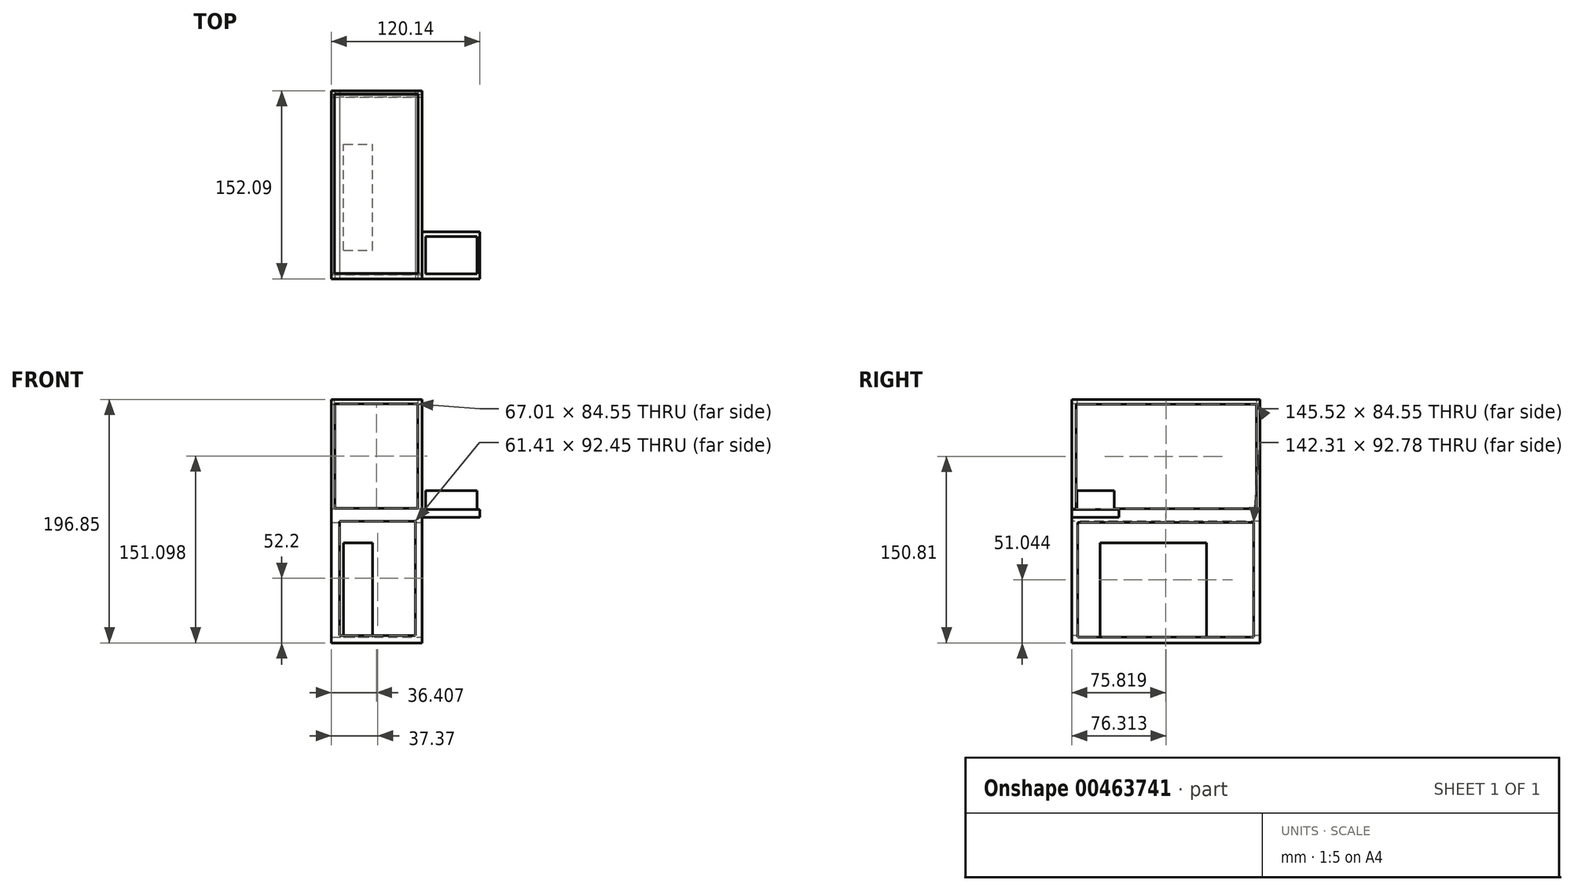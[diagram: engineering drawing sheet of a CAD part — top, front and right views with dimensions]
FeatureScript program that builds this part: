
annotation { "Feature Type Name" : "Feature", "Feature Type Description" : "" }
export const myFeature = defineFeature(function(context is Context, id is Id, definition is map)
    precondition{}
    {
        {
            var Q0;
            Q0=qCreatedBy(makeId("Top.planeOp"),FACE);
            var sketch = newSketch(context, id + "F0", { "sketchPlane" : qUnion([Q0])});
            skLineSegment(sketch, "E0", {"start": v(0, 0) * mm, "end": v(0, 75.66) * mm});
            skLineSegment(sketch, "E1", {"start": v(0, 75.66) * mm, "end": v(-73.36, 75.66) * mm});
            skLineSegment(sketch, "E2", {"start": v(-73.36, 75.66) * mm, "end": v(-73.36, -76.43) * mm});
            skLineSegment(sketch, "E3", {"start": v(-73.36, -76.43) * mm, "end": v(46.78, -76.43) * mm});
            skLineSegment(sketch, "E4", {"start": v(46.78, -76.43) * mm, "end": v(46.78, -38.34) * mm});
            skLineSegment(sketch, "E5", {"start": v(46.78, -38.34) * mm, "end": v(0, -38.34) * mm});
            skLineSegment(sketch, "E6", {"start": v(0, -38.34) * mm, "end": v(0, 0) * mm});
            skSolve(sketch);
        }
        {
            var Q0;
            Q0 = qSketchRegion(id + "F0", true);
            extrude(context, id + "F1", {"entities" : qUnion([Q0]), "depth" : 6.35 * mm});
        }
        {
            var Q0;
            Q0=makeQuery(id+"F1.opExtrude","CAP_FACE",FACE,{"disambiguationData":[OSD([sQuery(id+"F0.wireOp",EDGE,"E0"),sQuery(id+"F0.wireOp",EDGE,"E1"),sQuery(id+"F0.wireOp",EDGE,"E2"),sQuery(id+"F0.wireOp",EDGE,"E3"),sQuery(id+"F0.wireOp",EDGE,"E4"),sQuery(id+"F0.wireOp",EDGE,"E5"),sQuery(id+"F0.wireOp",EDGE,"E6")])],"isStart":false});
            var sketch = newSketch(context, id + "F2", { "sketchPlane" : qUnion([Q0])});
            skLineSegment(sketch, "E7.bottom", {"start": v(-73.36, 75.66) * mm, "end": v(0, 75.66) * mm});
            skLineSegment(sketch, "E7.top", {"start": v(-73.36, -76.43) * mm, "end": v(0, -76.43) * mm});
            skLineSegment(sketch, "E7.left", {"start": v(-73.36, 75.66) * mm, "end": v(-73.36, -76.43) * mm});
            skLineSegment(sketch, "E7.right", {"start": v(0, 75.66) * mm, "end": v(0, -76.43) * mm});
            skSolve(sketch);
        }
        {
            var Q0;
            Q0 = qSketchRegion(id + "F2", true);
            extrude(context, id + "F3", {"entities" : qUnion([Q0]), "operationType" : NewBodyOperationType.ADD, "depth" : 88.9 * mm});
        }
        {
            var Q0;
            Q0=makeQuery(id+"F3.boolean.opBoolean","MERGE",FACE,{"derivedFrom":[makeQuery(id+"F1.opExtrude","SWEPT_FACE",FACE,{"disambiguationData":[OSD([sQuery(id+"F0.wireOp",EDGE,"E3")])]}),makeQuery(id+"F3.opExtrude","SWEPT_FACE",FACE,{"disambiguationData":[OSD([sQuery(id+"F2.wireOp",EDGE,"E7.top")])]})]});
            var sketch = newSketch(context, id + "F4", { "sketchPlane" : qUnion([Q0])});
            skLineSegment(sketch, "E8.bottom", {"start": v(-70.46, 91.77) * mm, "end": v(-3.45, 91.77) * mm});
            skLineSegment(sketch, "E8.top", {"start": v(-70.46, 7.22) * mm, "end": v(-3.45, 7.22) * mm});
            skLineSegment(sketch, "E8.left", {"start": v(-70.46, 91.77) * mm, "end": v(-70.46, 7.22) * mm});
            skLineSegment(sketch, "E8.right", {"start": v(-3.45, 91.77) * mm, "end": v(-3.45, 7.22) * mm});
            skSolve(sketch);
        }
        {
            var Q0;
            Q0=makeQuery(id+"F4.imprint","IMPRINT",FACE,{"disambiguationData":[TD([[makeQuery(id+"F4.imprint","IMPRINT",EDGE,{"derivedFrom":sQuery(id+"F4.wireOp",EDGE,"E8.bottom")}),-1.0]])]});
            extrude(context, id + "F5", {"entities" : qUnion([Q0]), "operationType" : NewBodyOperationType.REMOVE, "endBound" : BoundingType.THROUGH_ALL, "oppositeDirection" : true, "depth" : 25.4 * mm});
        }
        {
            var Q0;
            Q0=makeQuery(id+"F3.boolean.opBoolean","MERGE",FACE,{"derivedFrom":[makeQuery(id+"F1.opExtrude","SWEPT_FACE",FACE,{"disambiguationData":[OSD([sQuery(id+"F0.wireOp",EDGE,"E0"),sQuery(id+"F0.wireOp",EDGE,"E6")])]}),makeQuery(id+"F3.opExtrude","SWEPT_FACE",FACE,{"disambiguationData":[OSD([sQuery(id+"F2.wireOp",EDGE,"E7.right")])]})]});
            var sketch = newSketch(context, id + "F6", { "sketchPlane" : qUnion([Q0])});
            skLineSegment(sketch, "E9.bottom", {"start": v(-72.88, 91.48) * mm, "end": v(72.64, 91.48) * mm});
            skLineSegment(sketch, "E9.top", {"start": v(-72.88, 6.94) * mm, "end": v(72.64, 6.94) * mm});
            skLineSegment(sketch, "E9.left", {"start": v(-72.88, 91.48) * mm, "end": v(-72.88, 6.94) * mm});
            skLineSegment(sketch, "E9.right", {"start": v(72.64, 91.48) * mm, "end": v(72.64, 6.94) * mm});
            skSolve(sketch);
        }
        {
            var Q0;
            Q0 = qSketchRegion(id + "F6", true);
            extrude(context, id + "F7", {"entities" : qUnion([Q0]), "operationType" : NewBodyOperationType.REMOVE, "endBound" : BoundingType.THROUGH_ALL, "oppositeDirection" : true, "depth" : 25.4 * mm});
        }
        {
            var Q0;
            Q0=makeQuery(id+"F1.opExtrude","CAP_FACE",FACE,{"disambiguationData":[OSD([sQuery(id+"F0.wireOp",EDGE,"E0"),sQuery(id+"F0.wireOp",EDGE,"E1"),sQuery(id+"F0.wireOp",EDGE,"E2"),sQuery(id+"F0.wireOp",EDGE,"E3"),sQuery(id+"F0.wireOp",EDGE,"E4"),sQuery(id+"F0.wireOp",EDGE,"E5"),sQuery(id+"F0.wireOp",EDGE,"E6")])],"isStart":true});
            var sketch = newSketch(context, id + "F8", { "sketchPlane" : qUnion([Q0])});
            skLineSegment(sketch, "E10.bottom", {"start": v(-73.36, 76.43) * mm, "end": v(0, 76.43) * mm});
            skLineSegment(sketch, "E10.top", {"start": v(-73.36, -75.66) * mm, "end": v(0, -75.66) * mm});
            skLineSegment(sketch, "E10.left", {"start": v(-73.36, 76.43) * mm, "end": v(-73.36, -75.66) * mm});
            skLineSegment(sketch, "E10.right", {"start": v(0, 76.43) * mm, "end": v(0, -75.66) * mm});
            skSolve(sketch);
        }
        {
            var Q0;
            {var subQ2=sQuery(id+"F8.wireOp",EDGE,"E10.bottom");Q0=makeQuery(id+"F8.imprint","IMPRINT",FACE,{"disambiguationData":[TD([[makeQuery(id+"F8.imprint","IMPRINT",EDGE,{"derivedFrom":subQ2}),-1.0]])]});}
            extrude(context, id + "F9", {"entities" : qUnion([Q0]), "operationType" : NewBodyOperationType.ADD, "depth" : 101.6 * mm});
        }
        {
            var Q0;
            Q0=makeQuery(id+"F9.boolean.opBoolean","MERGE",FACE,{"derivedFrom":[makeQuery(id+"F3.boolean.opBoolean","MERGE",FACE,{"derivedFrom":[makeQuery(id+"F1.opExtrude","SWEPT_FACE",FACE,{"disambiguationData":[OSD([sQuery(id+"F0.wireOp",EDGE,"E3")])]}),makeQuery(id+"F3.opExtrude","SWEPT_FACE",FACE,{"disambiguationData":[OSD([sQuery(id+"F2.wireOp",EDGE,"E7.top")])]})]}),makeQuery(id+"F9.opExtrude","SWEPT_FACE",FACE,{"disambiguationData":[OSD([sQuery(id+"F8.wireOp",EDGE,"E10.bottom")])]})]});
            var sketch = newSketch(context, id + "F10", { "sketchPlane" : qUnion([Q0])});
            skLineSegment(sketch, "E11.bottom", {"start": v(-66.7, -3.17) * mm, "end": v(-5.28, -3.17) * mm});
            skLineSegment(sketch, "E11.top", {"start": v(-66.7, -95.63) * mm, "end": v(-5.28, -95.63) * mm});
            skLineSegment(sketch, "E11.left", {"start": v(-66.7, -3.17) * mm, "end": v(-66.7, -95.63) * mm});
            skLineSegment(sketch, "E11.right", {"start": v(-5.28, -3.17) * mm, "end": v(-5.28, -95.63) * mm});
            skSolve(sketch);
        }
        {
            var Q0;
            Q0=makeQuery(id+"F10.imprint","IMPRINT",FACE,{"disambiguationData":[TD([[makeQuery(id+"F10.imprint","IMPRINT",EDGE,{"derivedFrom":sQuery(id+"F10.wireOp",EDGE,"E11.bottom")}),-1.0]])]});
            extrude(context, id + "F11", {"entities" : qUnion([Q0]), "operationType" : NewBodyOperationType.REMOVE, "endBound" : BoundingType.THROUGH_ALL, "oppositeDirection" : true, "depth" : 25.4 * mm});
        }
        {
            var Q0;
            Q0=makeQuery(id+"F9.boolean.opBoolean","MERGE",FACE,{"derivedFrom":[makeQuery(id+"F3.boolean.opBoolean","MERGE",FACE,{"derivedFrom":[makeQuery(id+"F1.opExtrude","SWEPT_FACE",FACE,{"disambiguationData":[OSD([sQuery(id+"F0.wireOp",EDGE,"E0"),sQuery(id+"F0.wireOp",EDGE,"E6")])]}),makeQuery(id+"F3.opExtrude","SWEPT_FACE",FACE,{"disambiguationData":[OSD([sQuery(id+"F2.wireOp",EDGE,"E7.right")])]})]}),makeQuery(id+"F9.opExtrude","SWEPT_FACE",FACE,{"disambiguationData":[OSD([sQuery(id+"F8.wireOp",EDGE,"E10.right")])]})]});
            var sketch = newSketch(context, id + "F12", { "sketchPlane" : qUnion([Q0])});
            skLineSegment(sketch, "E12.bottom", {"start": v(-71.76, -4.17) * mm, "end": v(70.54, -4.17) * mm});
            skLineSegment(sketch, "E12.top", {"start": v(-71.76, -96.95) * mm, "end": v(70.54, -96.95) * mm});
            skLineSegment(sketch, "E12.left", {"start": v(-71.76, -4.17) * mm, "end": v(-71.76, -96.95) * mm});
            skLineSegment(sketch, "E12.right", {"start": v(70.54, -4.17) * mm, "end": v(70.54, -96.95) * mm});
            skSolve(sketch);
        }
        {
            var Q0;
            Q0=makeQuery(id+"F12.imprint","IMPRINT",FACE,{"disambiguationData":[TD([[makeQuery(id+"F12.imprint","IMPRINT",EDGE,{"derivedFrom":sQuery(id+"F12.wireOp",EDGE,"E12.bottom")}),-1.0]])]});
            extrude(context, id + "F13", {"entities" : qUnion([Q0]), "operationType" : NewBodyOperationType.REMOVE, "endBound" : BoundingType.THROUGH_ALL, "oppositeDirection" : true, "depth" : 25.4 * mm});
        }
        {
            var Q0;
            Q0=makeQuery(id+"F1.opExtrude","CAP_FACE",FACE,{"disambiguationData":[OSD([sQuery(id+"F0.wireOp",EDGE,"E0"),sQuery(id+"F0.wireOp",EDGE,"E1"),sQuery(id+"F0.wireOp",EDGE,"E2"),sQuery(id+"F0.wireOp",EDGE,"E3"),sQuery(id+"F0.wireOp",EDGE,"E4"),sQuery(id+"F0.wireOp",EDGE,"E5"),sQuery(id+"F0.wireOp",EDGE,"E6")])],"isStart":false});
            var sketch = newSketch(context, id + "F14", { "sketchPlane" : qUnion([Q0])});
            skLineSegment(sketch, "E13.bottom", {"start": v(2.82, -42.1) * mm, "end": v(44.55, -42.1) * mm});
            skLineSegment(sketch, "E13.top", {"start": v(2.82, -72.31) * mm, "end": v(44.55, -72.31) * mm});
            skLineSegment(sketch, "E13.left", {"start": v(2.82, -42.1) * mm, "end": v(2.82, -72.31) * mm});
            skLineSegment(sketch, "E13.right", {"start": v(44.55, -42.1) * mm, "end": v(44.55, -72.31) * mm});
            skSolve(sketch);
        }
        {
            var Q0;
            Q0=makeQuery(id+"F14.imprint","IMPRINT",FACE,{"disambiguationData":[TD([[makeQuery(id+"F14.imprint","IMPRINT",EDGE,{"derivedFrom":sQuery(id+"F14.wireOp",EDGE,"E13.bottom")}),-1.0]])]});
            extrude(context, id + "F15", {"entities" : qUnion([Q0]), "depth" : 15.24 * mm});
        }
        {
            var Q0;
            Q0=makeQuery(id+"F13.boolean.opBoolean","COPY",FACE,{"derivedFrom":makeQuery(id+"F13.opExtrude","SWEPT_FACE",FACE,{"disambiguationData":[OSD([sQuery(id+"F12.wireOp",EDGE,"E12.top")])]})});
            var sketch = newSketch(context, id + "F16", { "sketchPlane" : qUnion([Q0])});
            skLineSegment(sketch, "E14.bottom", {"start": v(-63.37, -53.44) * mm, "end": v(-40.04, -53.44) * mm});
            skLineSegment(sketch, "E14.top", {"start": v(-63.37, 32.38) * mm, "end": v(-40.04, 32.38) * mm});
            skLineSegment(sketch, "E14.left", {"start": v(-63.37, -53.44) * mm, "end": v(-63.37, 32.38) * mm});
            skLineSegment(sketch, "E14.right", {"start": v(-40.04, -53.44) * mm, "end": v(-40.04, 32.38) * mm});
            skSolve(sketch);
        }
        {
            var Q0;
            Q0 = qSketchRegion(id + "F16", true);
            extrude(context, id + "F17", {"entities" : qUnion([Q0]), "depth" : 76.2 * mm});
        }
        {
            var Q0;
            Q0=makeQuery(id+"F3.opExtrude","CAP_FACE",FACE,{"disambiguationData":[OSD([sQuery(id+"F2.wireOp",EDGE,"E7.bottom"),sQuery(id+"F2.wireOp",EDGE,"E7.top"),sQuery(id+"F2.wireOp",EDGE,"E7.left"),sQuery(id+"F2.wireOp",EDGE,"E7.right")])],"isStart":false});
            var sketch = newSketch(context, id + "F18", { "sketchPlane" : qUnion([Q0])});
            skLineSegment(sketch, "E15.bottom", {"start": v(-70.92, 73.1) * mm, "end": v(-3.33, 73.1) * mm});
            skLineSegment(sketch, "E15.top", {"start": v(-70.92, -72.05) * mm, "end": v(-3.33, -72.05) * mm});
            skLineSegment(sketch, "E15.left", {"start": v(-70.92, 73.1) * mm, "end": v(-70.92, -72.05) * mm});
            skLineSegment(sketch, "E15.right", {"start": v(-3.33, 73.1) * mm, "end": v(-3.33, -72.05) * mm});
            skSolve(sketch);
        }
        {
            var Q0;
            Q0=makeQuery(id+"F18.imprint","IMPRINT",FACE,{"disambiguationData":[TD([[makeQuery(id+"F18.imprint","IMPRINT",EDGE,{"derivedFrom":sQuery(id+"F18.wireOp",EDGE,"E15.bottom")}),-1.0]])]});
            extrude(context, id + "F19", {"entities" : qUnion([Q0]), "operationType" : NewBodyOperationType.REMOVE, "oppositeDirection" : true, "depth" : 25.4 * mm});
        }
    });
